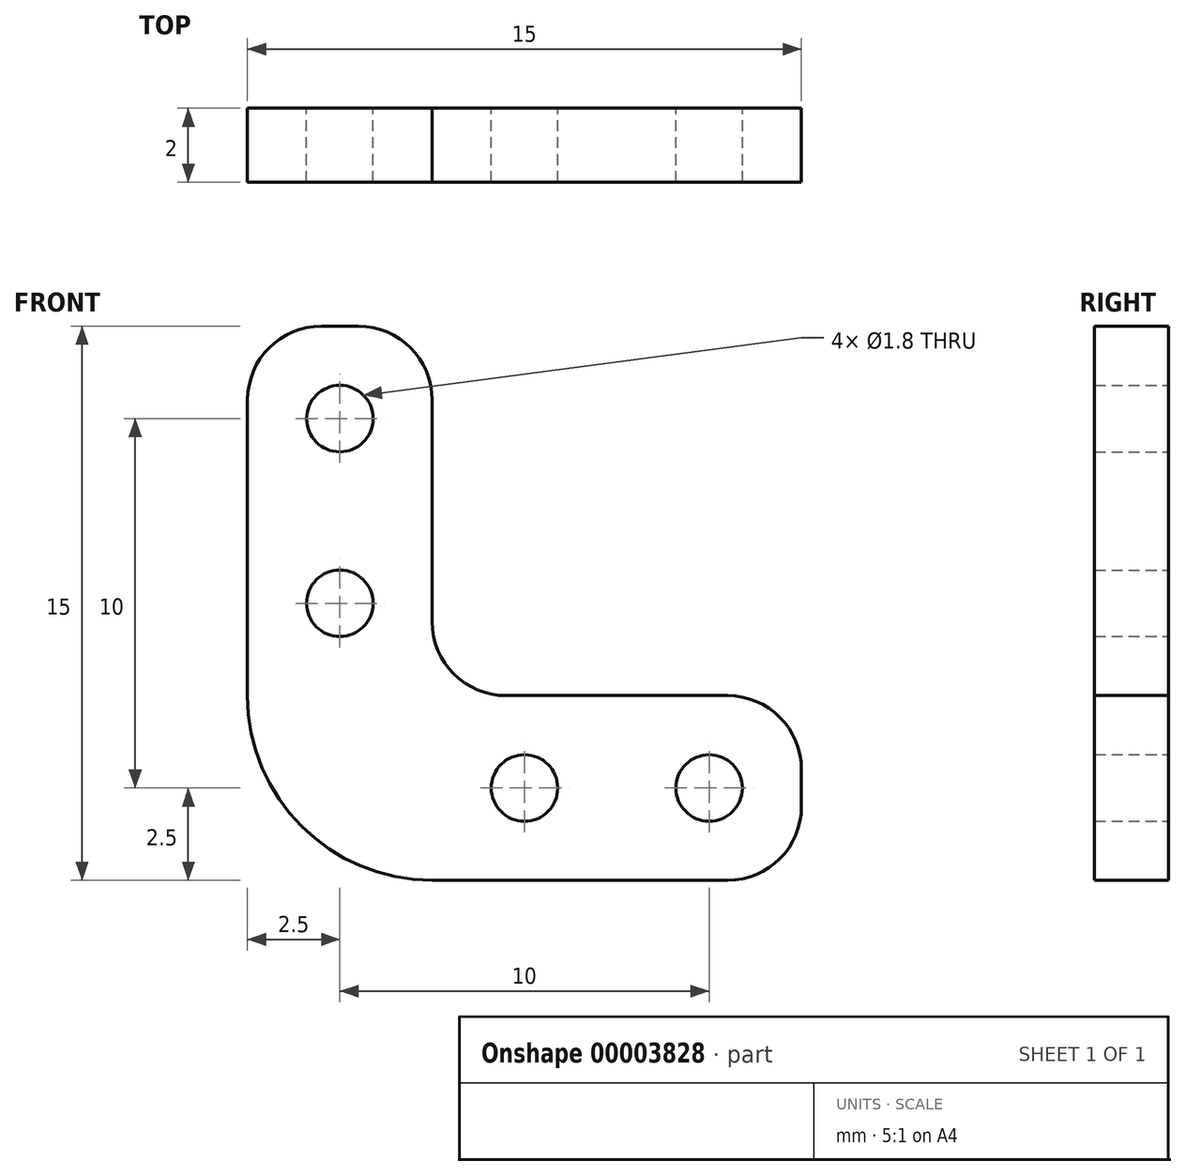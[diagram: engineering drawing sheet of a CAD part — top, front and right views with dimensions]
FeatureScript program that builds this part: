
annotation { "Feature Type Name" : "Feature", "Feature Type Description" : "" }
export const myFeature = defineFeature(function(context is Context, id is Id, definition is map)
    precondition{}
    {
        {
            var Q0;
            Q0=qCreatedBy(makeId("Front.planeOp"),FACE);
            var sketch = newSketch(context, id + "F0", { "sketchPlane" : qUnion([Q0])});
            skLineSegment(sketch, "E0", {"start": v(0, 0) * mm, "end": v(15, 0) * mm});
            skLineSegment(sketch, "E1", {"start": v(15, 0) * mm, "end": v(15, 5) * mm});
            skLineSegment(sketch, "E2", {"start": v(15, 5) * mm, "end": v(5, 5) * mm});
            skLineSegment(sketch, "E3", {"start": v(5, 5) * mm, "end": v(5, 15) * mm});
            skLineSegment(sketch, "E4", {"start": v(5, 15) * mm, "end": v(0, 15) * mm});
            skLineSegment(sketch, "E5", {"start": v(0, 15) * mm, "end": v(0, 0) * mm});
            skLineSegment(sketch, "E6", {"start": v(2.5, 15) * mm, "end": v(2.5, 2.5) * mm, "construction": true});
            skLineSegment(sketch, "E7", {"start": v(15, 2.5) * mm, "end": v(2.5, 2.5) * mm, "construction": true});
            skCircle(sketch, "E8", {"center": v(12.5, 2.5) * mm, "radius": 0.9 * mm});
            skCircle(sketch, "E9", {"center": v(7.5, 2.5) * mm, "radius": 0.9 * mm});
            skCircle(sketch, "E10", {"center": v(2.5, 12.5) * mm, "radius": 0.9 * mm});
            skCircle(sketch, "E11", {"center": v(2.5, 7.5) * mm, "radius": 0.9 * mm});
            skSolve(sketch);
        }
        {
            var Q0;
            Q0=makeQuery(id+"F0.imprint","IMPRINT",FACE,{"disambiguationData":[TD([[makeQuery(id+"F0.imprint","IMPRINT",EDGE,{"derivedFrom":sQuery(id+"F0.wireOp",EDGE,"E0")}),1.0]])]});
            extrude(context, id + "F1", {"entities" : qUnion([Q0]), "depth" : 2 * mm});
        }
        {
            var Q0;
            Q0=makeQuery(id+"F1.opExtrude","SWEPT_EDGE",EDGE,{"disambiguationData":[OSD([sQuery(id+"F0.wireOp",EDGE,"E0"),sQuery(id+"F0.wireOp",EDGE,"E5")])]});
            fillet(context, id + "F2", {"entities" : qUnion([Q0]), "radius" : 5 * mm, "tangentPropagation" : true, "allowEdgeOverflow" : false});
        }
        {
            var Q0;
            Q0=makeQuery(id+"F1.opExtrude","SWEPT_EDGE",EDGE,{"disambiguationData":[OSD([sQuery(id+"F0.wireOp",EDGE,"E2"),sQuery(id+"F0.wireOp",EDGE,"E3")])]});
            var Q1;
            Q1=makeQuery(id+"F1.opExtrude","SWEPT_EDGE",EDGE,{"disambiguationData":[OSD([sQuery(id+"F0.wireOp",EDGE,"E4"),sQuery(id+"F0.wireOp",EDGE,"E5")])]});
            var Q2;
            Q2=makeQuery(id+"F1.opExtrude","SWEPT_EDGE",EDGE,{"disambiguationData":[OSD([sQuery(id+"F0.wireOp",EDGE,"E3"),sQuery(id+"F0.wireOp",EDGE,"E4")])]});
            var Q3;
            Q3=makeQuery(id+"F1.opExtrude","SWEPT_EDGE",EDGE,{"disambiguationData":[OSD([sQuery(id+"F0.wireOp",EDGE,"E1"),sQuery(id+"F0.wireOp",EDGE,"E2")])]});
            var Q4;
            Q4=makeQuery(id+"F1.opExtrude","SWEPT_EDGE",EDGE,{"disambiguationData":[OSD([sQuery(id+"F0.wireOp",EDGE,"E0"),sQuery(id+"F0.wireOp",EDGE,"E1")])]});
            fillet(context, id + "F3", {"entities" : qUnion([Q0, Q1, Q2, Q3, Q4]), "radius" : 2 * mm, "tangentPropagation" : true, "allowEdgeOverflow" : false});
        }
    });
